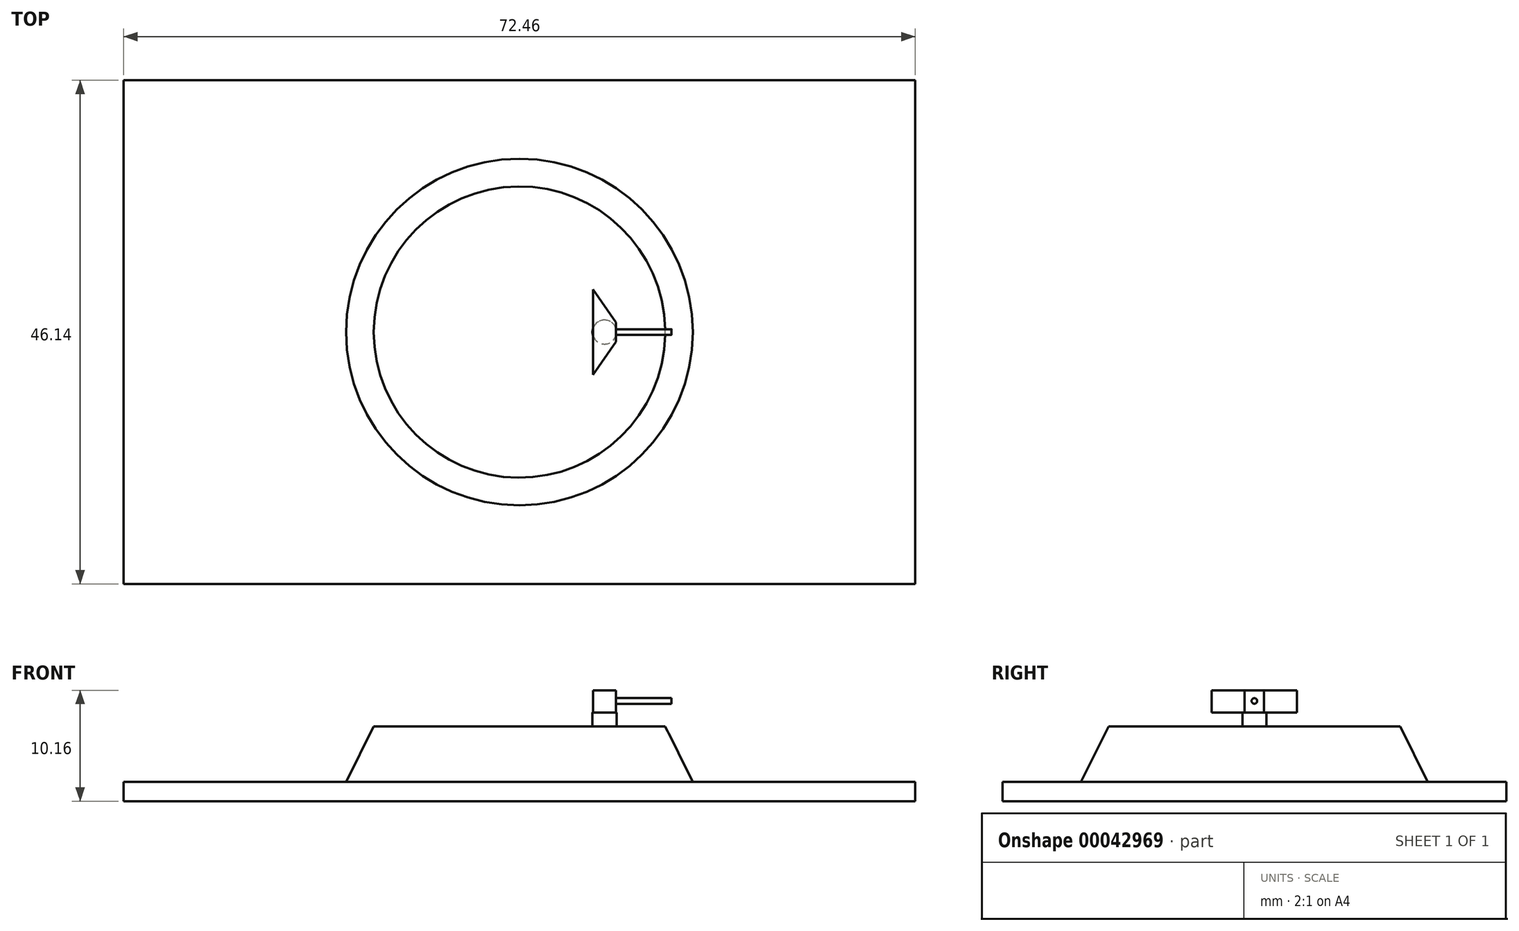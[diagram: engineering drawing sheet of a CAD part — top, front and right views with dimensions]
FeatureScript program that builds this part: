
annotation { "Feature Type Name" : "Feature", "Feature Type Description" : "" }
export const myFeature = defineFeature(function(context is Context, id is Id, definition is map)
    precondition{}
    {
        {
            var Q0;
            Q0=qCreatedBy(makeId("Top.planeOp"),FACE);
            var sketch = newSketch(context, id + "F0", { "sketchPlane" : qUnion([Q0])});
            skLineSegment(sketch, "E0.rect.bottom", {"start": v(-36.23, -23.07) * mm, "end": v(36.23, -23.07) * mm});
            skLineSegment(sketch, "E0.rect.top", {"start": v(-36.23, 23.07) * mm, "end": v(36.23, 23.07) * mm});
            skLineSegment(sketch, "E0.rect.left", {"start": v(-36.23, -23.07) * mm, "end": v(-36.23, 23.07) * mm});
            skLineSegment(sketch, "E0.rect.right", {"start": v(36.23, -23.07) * mm, "end": v(36.23, 23.07) * mm});
            skPoint(sketch, "E0.rect.middle", {"position": v(0, 0) * mm});
            skSolve(sketch);
        }
        {
            var Q0;
            Q0=makeQuery(id+"F0.imprint","IMPRINT",FACE,{"disambiguationData":[TD([[makeQuery(id+"F0.imprint","IMPRINT",EDGE,{"derivedFrom":sQuery(id+"F0.wireOp",EDGE,"E0.rect.bottom")}),1.0]])]});
            extrude(context, id + "F1", {"entities" : qUnion([Q0]), "depth" : 1.78 * mm});
        }
        {
            var Q0;
            Q0=makeQuery(id+"F1.opExtrude","CAP_FACE",FACE,{"disambiguationData":[OSD([sQuery(id+"F0.wireOp",EDGE,"E0.rect.bottom"),sQuery(id+"F0.wireOp",EDGE,"E0.rect.top"),sQuery(id+"F0.wireOp",EDGE,"E0.rect.left"),sQuery(id+"F0.wireOp",EDGE,"E0.rect.right")])],"isStart":false});
            var sketch = newSketch(context, id + "F2", { "sketchPlane" : qUnion([Q0])});
            skCircle(sketch, "E1", {"center": v(0, 0) * mm, "radius": 15.88 * mm});
            skSolve(sketch);
        }
        {
            var Q0;
            Q0=makeQuery(id+"F2.imprint","IMPRINT",FACE,{"disambiguationData":[TD([[makeQuery(id+"F2.imprint","IMPRINT",EDGE,{"derivedFrom":sQuery(id+"F2.wireOp",EDGE,"E1")}),1.0]])]});
            cPlane(context, id + "F3", {"entities" : qUnion([Q0]), "cplaneType" : CPlaneType.OFFSET, "offset" : 5.08 * mm, "width" : 152.4 * mm, "height" : 152.4 * mm});
        }
        {
            var Q0;
            Q0=qCreatedBy(id+"F3.planeOp",FACE);
            var sketch = newSketch(context, id + "F4", { "sketchPlane" : qUnion([Q0])});
            skCircle(sketch, "E2", {"center": v(0, 0) * mm, "radius": 13.34 * mm});
            skSolve(sketch);
        }
        {
            var Q1;
            Q1=makeQuery(id+"F2.imprint","IMPRINT",FACE,{"disambiguationData":[TD([[makeQuery(id+"F2.imprint","IMPRINT",EDGE,{"derivedFrom":sQuery(id+"F2.wireOp",EDGE,"E1")}),1.0]])]});
            var Q2;
            Q2=makeQuery(id+"F4.imprint","IMPRINT",FACE,{"disambiguationData":[TD([[makeQuery(id+"F4.imprint","IMPRINT",EDGE,{"derivedFrom":sQuery(id+"F4.wireOp",EDGE,"E2")}),1.0]])]});
            loft(context, id + "F5", {"operationType" : NewBodyOperationType.ADD, "sheetProfilesArray" : [{ "sheetProfileEntities" : qUnion([Q1]) }, { "sheetProfileEntities" : qUnion([Q2]) }]});
        }
        {
            var Q0;
            Q0=makeQuery(id+"F4.imprint","IMPRINT",FACE,{"disambiguationData":[TD([[makeQuery(id+"F4.imprint","IMPRINT",EDGE,{"derivedFrom":sQuery(id+"F4.wireOp",EDGE,"E2")}),1.0]])]});
            var sketch = newSketch(context, id + "F6", { "sketchPlane" : qUnion([Q0])});
            skCircle(sketch, "E3", {"center": v(7.79, 0) * mm, "radius": 1.1 * mm});
            skSolve(sketch);
        }
        {
            var Q0;
            Q0=makeQuery(id+"F6.imprint","IMPRINT",FACE,{"disambiguationData":[TD([[makeQuery(id+"F6.imprint","IMPRINT",EDGE,{"derivedFrom":sQuery(id+"F6.wireOp",EDGE,"E3")}),1.0]])]});
            extrude(context, id + "F7", {"entities" : qUnion([Q0]), "operationType" : NewBodyOperationType.ADD, "depth" : 1.27 * mm});
        }
        {
            var Q0;
            Q0=makeQuery(id+"F7.opExtrude","CAP_FACE",FACE,{"disambiguationData":[OSD([sQuery(id+"F6.wireOp",EDGE,"E3")])],"isStart":false});
            var sketch = newSketch(context, id + "F8", { "sketchPlane" : qUnion([Q0])});
            skLineSegment(sketch, "E4.rect.bottom", {"start": v(6.73, -5.97) * mm, "end": v(8.85, -5.97) * mm});
            skLineSegment(sketch, "E4.rect.top", {"start": v(6.73, 5.97) * mm, "end": v(8.85, 5.97) * mm});
            skLineSegment(sketch, "E4.rect.left", {"start": v(6.73, -5.97) * mm, "end": v(6.73, 5.97) * mm});
            skLineSegment(sketch, "E4.rect.right", {"start": v(8.85, -5.97) * mm, "end": v(8.85, 5.97) * mm});
            skPoint(sketch, "E4.rect.middle", {"position": v(7.79, 0) * mm});
            skSolve(sketch);
        }
        {
            var Q0;
            {var subQ3=sQuery(id+"F8.wireOp",EDGE,"E4.rect.bottom");Q0=makeQuery(id+"F8.imprint","IMPRINT",FACE,{"disambiguationData":[TD([[makeQuery(id+"F8.imprint","IMPRINT",EDGE,{"derivedFrom":subQ3}),1.0]])]});}
            var Q1;
            {var subQ3=sQuery(id+"F8.wireOp",EDGE,"E4.rect.top");Q1=makeQuery(id+"F8.imprint","IMPRINT",FACE,{"disambiguationData":[TD([[makeQuery(id+"F8.imprint","IMPRINT",EDGE,{"derivedFrom":subQ3}),-1.0]])]});}
            var Q2;
            {var subQ0=makeQuery(id+"F7.opExtrude","CAP_EDGE",EDGE,{"disambiguationData":[OSD([sQuery(id+"F6.wireOp",EDGE,"E3")])],"isStart":false});var subQ3=sQuery(id+"F8.wireOp",EDGE,"E4.rect.left");var subQ6=makeQuery(id+"F8.imprint","INTERSECT",VERTEX,{"disambiguationData":[OD(0.0)],"derivedFrom":[subQ0,subQ3]});Q2=makeQuery(id+"F8.imprint","IMPRINT",FACE,{"disambiguationData":[TD([[makeQuery(id+"F8.imprint","IMPRINT",EDGE,{"disambiguationData":[TD([[subQ6,-1.0]])],"derivedFrom":subQ3}),-1.0]])]});}
            extrude(context, id + "F9", {"entities" : qUnion([Q0, Q1, Q2]), "operationType" : NewBodyOperationType.ADD, "depth" : 2.03 * mm});
        }
        {
            var Q0;
            Q0=makeQuery(id+"F9.opExtrude","SWEPT_EDGE",EDGE,{"disambiguationData":[OSD([sQuery(id+"F8.wireOp",EDGE,"E4.rect.bottom"),sQuery(id+"F8.wireOp",EDGE,"E4.rect.right")])]});
            var Q1;
            Q1=makeQuery(id+"F9.opExtrude","SWEPT_EDGE",EDGE,{"disambiguationData":[OSD([sQuery(id+"F8.wireOp",EDGE,"E4.rect.top"),sQuery(id+"F8.wireOp",EDGE,"E4.rect.right")])]});
            chamfer(context, id + "F10", {"entities" : qUnion([Q0, Q1]), "chamferType" : ChamferType.OFFSET_ANGLE, "width" : 5.08 * mm, "oppositeDirection" : false, "angle" : 35 * degree, "tangentPropagation" : true});
        }
        {
            var Q0;
            Q0=makeQuery(id+"F9.opExtrude","SWEPT_FACE",FACE,{"disambiguationData":[OSD([sQuery(id+"F8.wireOp",EDGE,"E4.rect.right")])]});
            var sketch = newSketch(context, id + "F11", { "sketchPlane" : qUnion([Q0])});
            skCircle(sketch, "E5", {"center": v(0, 9.18) * mm, "radius": 0.26 * mm});
            skSolve(sketch);
        }
        {
            var Q0;
            Q0=makeQuery(id+"F11.imprint","IMPRINT",FACE,{"disambiguationData":[TD([[makeQuery(id+"F11.imprint","IMPRINT",EDGE,{"derivedFrom":sQuery(id+"F11.wireOp",EDGE,"E5")}),1.0]])]});
            extrude(context, id + "F12", {"entities" : qUnion([Q0]), "operationType" : NewBodyOperationType.ADD, "depth" : 5.08 * mm});
        }
    });
